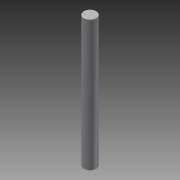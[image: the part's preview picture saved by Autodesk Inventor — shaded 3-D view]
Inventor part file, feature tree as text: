
AUTODESK INVENTOR PART (.ipt)
format: ipt  version: 2014 (Build 180170000, 170)  size: 65,536 bytes
history: native  units: in
note: dims shown in document units (in); Inventor stores cm internally (conversion verified against a paired STEP export)
features: extrude x1, sketch x1
ambient origin geometry x8: Origin, YZ Plane, XZ Plane, XY Plane, X Axis, Y Axis, Z Axis, Center Point
bodies: Solid1 (feature_tree)
feature tree (2):
  extrude  "Extrusion1"  Depth=2.0in TaperAngle=0.0deg
  sketch  "Sketch1"  dims[d0=0.19in d1=2.0in d2=0.0in]
